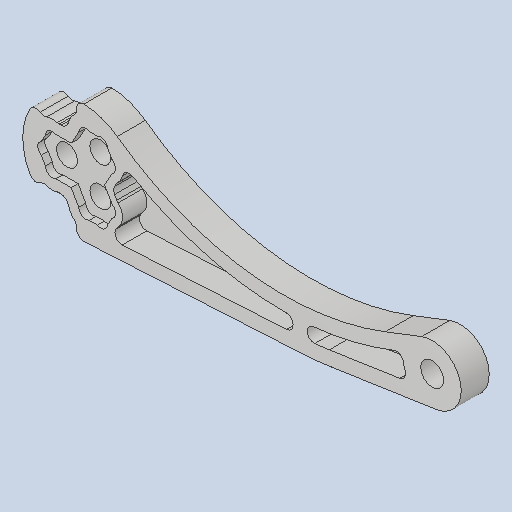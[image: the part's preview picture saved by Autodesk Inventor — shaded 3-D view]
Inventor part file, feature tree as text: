
AUTODESK INVENTOR PART (.ipt)
format: ipt  version: 2023 (Build 270158030, 158C)  size: 1,325,056 bytes
history: native  units: mm
features: extrude x27, sketch x27, projected_geometry x17, other x16, fillet x7, reference x5, shell x1, hole x1
ambient origin geometry x8: Origin, YZ Plane, XZ Plane, XY Plane, X Axis, Y Axis, Z Axis, Center Point
bodies: Body1 (feature_tree)
feature tree (101):
  other  "ソリッド1"
  extrude  "押し出し1"  Depth=10.0mm
  extrude  "押し出し2"  Depth=3.3mm
  extrude  "押し出し3"  Depth=18.0mm
  sketch  "スケッチ6"
  shell  "シェル1"  Thickness=50.0mm
  extrude  "押し出し4"  Depth=6.0mm
  extrude  "押し出し5"  Depth=9.0mm
  fillet  "フィレット1"  Radius=9.0mm
  fillet  "フィレット3"  Radius=4.0mm
  sketch  "スケッチ10"
  extrude  "押し出し7"  Depth=4.0mm
  sketch  "スケッチ13"
  sketch  "スケッチ14"
  extrude  "押し出し8"  Depth=5.0mm TaperAngle=0.0deg
  hole  "穴1"  [1 undecoded]
  extrude  "押し出し9"  Depth=7.0mm
  sketch  "スケッチ16"
  extrude  "押し出し10"  Depth=2.1mm
  extrude  "押し出し11"  Depth=2.1mm
  extrude  "押し出し12"  Depth=2.1mm
  extrude  "押し出し13"  Depth=2.1mm
  extrude  "押し出し14"  Depth=2.1mm
  extrude  "押し出し15"  Depth=2.1mm
  extrude  "押し出し16"  Depth=2.1mm
  extrude  "押し出し17"  Depth=2.1mm
  extrude  "押し出し18"  Depth=2.1mm
  fillet  "フィレット4"  Radius=2.1mm
  extrude  "押し出し19"  Depth=2.1mm
  fillet  "フィレット5"  Radius=2.1mm
  sketch  "スケッチ25"
  extrude  "押し出し20"  TaperAngle=60.0deg  [1 undecoded]
  extrude  "押し出し21"  TaperAngle=60.0deg  [1 undecoded]
  sketch  "スケッチ26"
  extrude  "押し出し22"  TaperAngle=60.0deg  [1 undecoded]
  extrude  "押し出し23"  TaperAngle=60.0deg  [1 undecoded]
  extrude  "押し出し24"  Depth=2.0mm TaperAngle=0.0deg
  fillet  "フィレット6"  Radius=25.0mm
  sketch  "スケッチ29"
  extrude  "押し出し25"  Depth=5.0mm TaperAngle=0.0deg
  extrude  "押し出し26"  Depth=3.0mm
  extrude  "押し出し27"  Depth=5.0mm TaperAngle=0.0deg
  fillet  "フィレット7"  Radius=0.7mm
  extrude  "押し出し28"  Depth=2.0mm
  fillet  "フィレット8"  Radius=1.0mm
  sketch  "スケッチ1"
  sketch  "スケッチ2"
  sketch  "スケッチ3"
  reference  "参照1"
  reference  "参照9"
  reference  "参照10"
  reference  "参照11"
  reference  "参照12"
  sketch  "スケッチ7"
  sketch  "スケッチ8"
  projected_geometry  "投影ループ1"
  projected_geometry  "投影ループ2"
  projected_geometry  "投影ループ3"
  projected_geometry  "投影ループ4"
  projected_geometry  "投影ループ6"
  sketch  "スケッチ12"
  projected_geometry  "投影ループ7"
  projected_geometry  "投影ループ8"
  sketch  "スケッチ15"
  sketch  "スケッチ17"
  sketch  "スケッチ18"
  sketch  "スケッチ19"
  sketch  "スケッチ20"
  projected_geometry  "投影ループ9"
  sketch  "スケッチ21"
  projected_geometry  "投影ループ10"
  sketch  "スケッチ22"
  projected_geometry  "投影ループ11"
  projected_geometry  "投影ループ12"
  sketch  "スケッチ23"
  projected_geometry  "投影ループ13"
  sketch  "スケッチ24"
  projected_geometry  "投影ループ14"
  projected_geometry  "投影ループ15"
  projected_geometry  "投影ループ16"
  sketch  "スケッチ27"
  projected_geometry  "投影ループ17"
  sketch  "スケッチ28"
  projected_geometry  "投影ループ18"
  sketch  "スケッチ30"
  sketch  "スケッチ31"
  other  "<userpath>\Documents\SRDC\SRDC\Inventor_2017\2018年機体\2019年3年機体\アームロッドアセンブリ1.iam"
  other  "アームロッドアセンブリ1.iam"
  other  "スペーサーm4,45:1"
  other  "スペーサーm4,06:1"
  other  "アームフレーム4.1:1"
  other  "スペーサーm4,45:2"
  other  "断面エッジを投影1"
  other  "断面エッジを投影2"
  other  "断面エッジを投影3"
  other  "断面エッジを投影4"
  other  "断面エッジを投影5"
  other  "断面エッジを投影6"
  other  "断面エッジを投影7"
  other  "断面エッジを投影8"
  other  "断面エッジを投影9"
note: 5 required parameter values undecoded (feature->parameter linkage not recoverable at this tier; creation-order binding heuristic only, values carry confidence <= 0.55)
